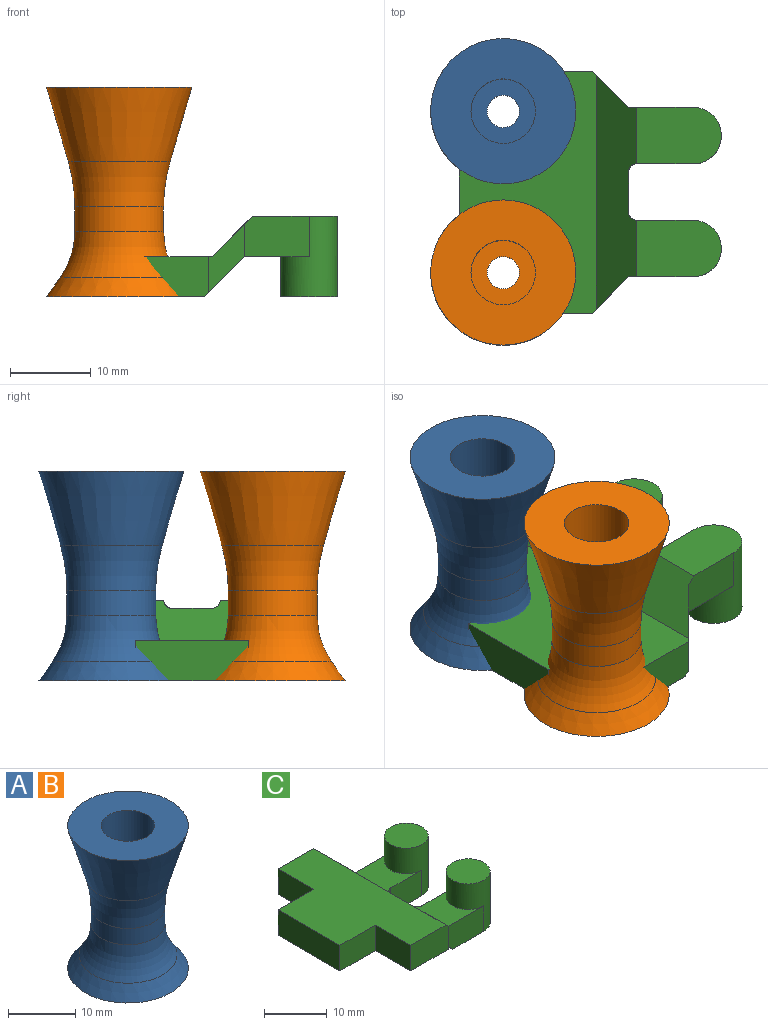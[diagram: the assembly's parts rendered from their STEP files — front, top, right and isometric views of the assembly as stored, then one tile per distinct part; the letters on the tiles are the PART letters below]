
ASSEMBLY  parts=3 mates=2
PART A: 10 faces, bbox 24.5x24.5x26 mm
  f0: cone r=5.5mm half-angle=16.3deg, axis (0,0,1), area 463.5mm2, adj f1,f9
  f1: plane 18x18mm, normal (0,0,1), area 204.2mm2, adj f0,f2
  f2: cylinder r=4mm len=18mm, axis (0,0,-1), area 452.4mm2, adj f1,f3
  f3: plane 8x8mm, normal (0,0,1), area 37.7mm2, adj f2,f4
  f4: cylinder r=2mm len=8mm, axis (0,0,-1), area 100.5mm2, adj f3,f5
  f5: plane 18x18mm, normal (0,0,-1), area 241.9mm2, adj f4,f6
  f6: cone r=9mm half-angle=35deg, axis (0,0,-1), area 151.2mm2, adj f5,f8
  f7: cylinder r=5.5mm len=11mm, axis (0,0,-1), area 103.3mm2, adj f8,f9
  f8: torus R=15.5mm, axis (0,0,-1), area 234.5mm2, adj f6,f7
  f9: torus R=25.5mm, axis (0,0,-1), area 205.7mm2, adj f0,f7
PART B: same geometry as A
PART C: 28 faces, bbox 32.5x30x10 mm
  f0: plane 8.5x5mm, normal (0,1,0), area 42.4mm2, adj f2,f4,f19,f20,f27
  f1: plane 8.5x5mm, normal (0,-1,0), area 42.4mm2, adj f2,f4,f19,f21,f25
  f2: plane 30x16mm, normal (0,0,1), area 352mm2, adj f0,f1,f3,f19,f24,f25,f26,f27
  f3: plane 14x5mm, normal (-1,0,0), area 70mm2, adj f2,f4,f24,f26
  f4: plane 30x17mm, normal (0,0,-1), area 381.7mm2, adj f0,f1,f3,f18,f20,f21,f24,f25
  f5: plane 5x4mm, normal (1,0,0), area 20mm2, adj f18,f19,f22,f23
  f6: plane 10.5x7mm, normal (0,0,-1), area 68.2mm2, adj f12,f16,f17,f18
  f7: plane 8x8mm, normal (0,0,1), area 37mm2, adj f10,f14,f15,f19,f22
  f8: plane 8x8mm, normal (0,0,1), area 37mm2, adj f12,f16,f17,f19,f23
  f9: plane 10.5x7mm, normal (0,0,-1), area 68.2mm2, adj f10,f14,f15,f18
  f10: cylinder r=3.5mm len=10mm, axis (0,0,-1), area 164.9mm2, adj f7,f9,f11,f14,f15
  f11: plane 7x7mm, normal (0,0,1), area 38.5mm2, adj f10
  f12: cylinder r=3.5mm len=10mm, axis (0,0,-1), area 164.9mm2, adj f6,f8,f13,f16,f17
  f13: plane 7x7mm, normal (0,0,1), area 38.5mm2, adj f12
  f14: plane 8x5mm, normal (0,1,0), area 39.5mm2, adj f7,f9,f10,f18,f20
  f15: plane 7x5mm, normal (0,-1,0), area 35mm2, adj f7,f9,f10,f22
  f16: plane 7x5mm, normal (0,1,0), area 35mm2, adj f6,f8,f12,f23
  f17: plane 8x5mm, normal (0,-1,0), area 39.5mm2, adj f6,f8,f12,f18,f21
  f18: plane 29x5mm, normal (-0.71,0,-0.71), area 161.8mm2, adj f4,f5,f6,f9,f14,f17,f20,f21
  f19: plane 30x5mm, normal (0.71,0,0.71), area 183.5mm2, adj f0,f1,f2,f5,f7,f8,f20,f21
  f20: plane 8.5x4.5mm, normal (0.71,0.71,0), area 25.6mm2, adj f0,f4,f14,f18,f19
  f21: plane 8.5x4.5mm, normal (0.71,-0.71,0), area 25.6mm2, adj f1,f4,f17,f18,f19
  f22: cylinder r=1mm len=5mm, axis (0,0,-1), area 6.9mm2, adj f5,f7,f15,f18
  f23: cylinder r=1mm len=5mm, axis (0,0,1), area 6.9mm2, adj f5,f8,f16,f18
  f24: plane 8x5mm, normal (0,-1,0), area 40mm2, adj f2,f3,f4,f25
  f25: plane 8x5mm, normal (-1,0,0), area 40mm2, adj f1,f2,f4,f24
  f26: plane 8x5mm, normal (0,1,0), area 40mm2, adj f2,f3,f4,f27
  f27: plane 8x5mm, normal (-1,0,0), area 40mm2, adj f0,f2,f4,f26
PLACE A rot(axis=(1,0,0),0deg) t=(7.09,55.37,5.89)mm
PLACE B rot(axis=(1,0,0),0deg) t=(7.09,35.37,5.89)mm
PLACE C rot(axis=(-1,0,0),180deg) t=(23.64,45.37,15.89)mm
MATE fastened C.f2 <-> B.f5  axis (0,0,-1) through (11.09,45.37,5.89)mm
MATE fastened A.f0 <-> B.f1  axis (0,0,1) through (7.09,55.37,31.89)mm
